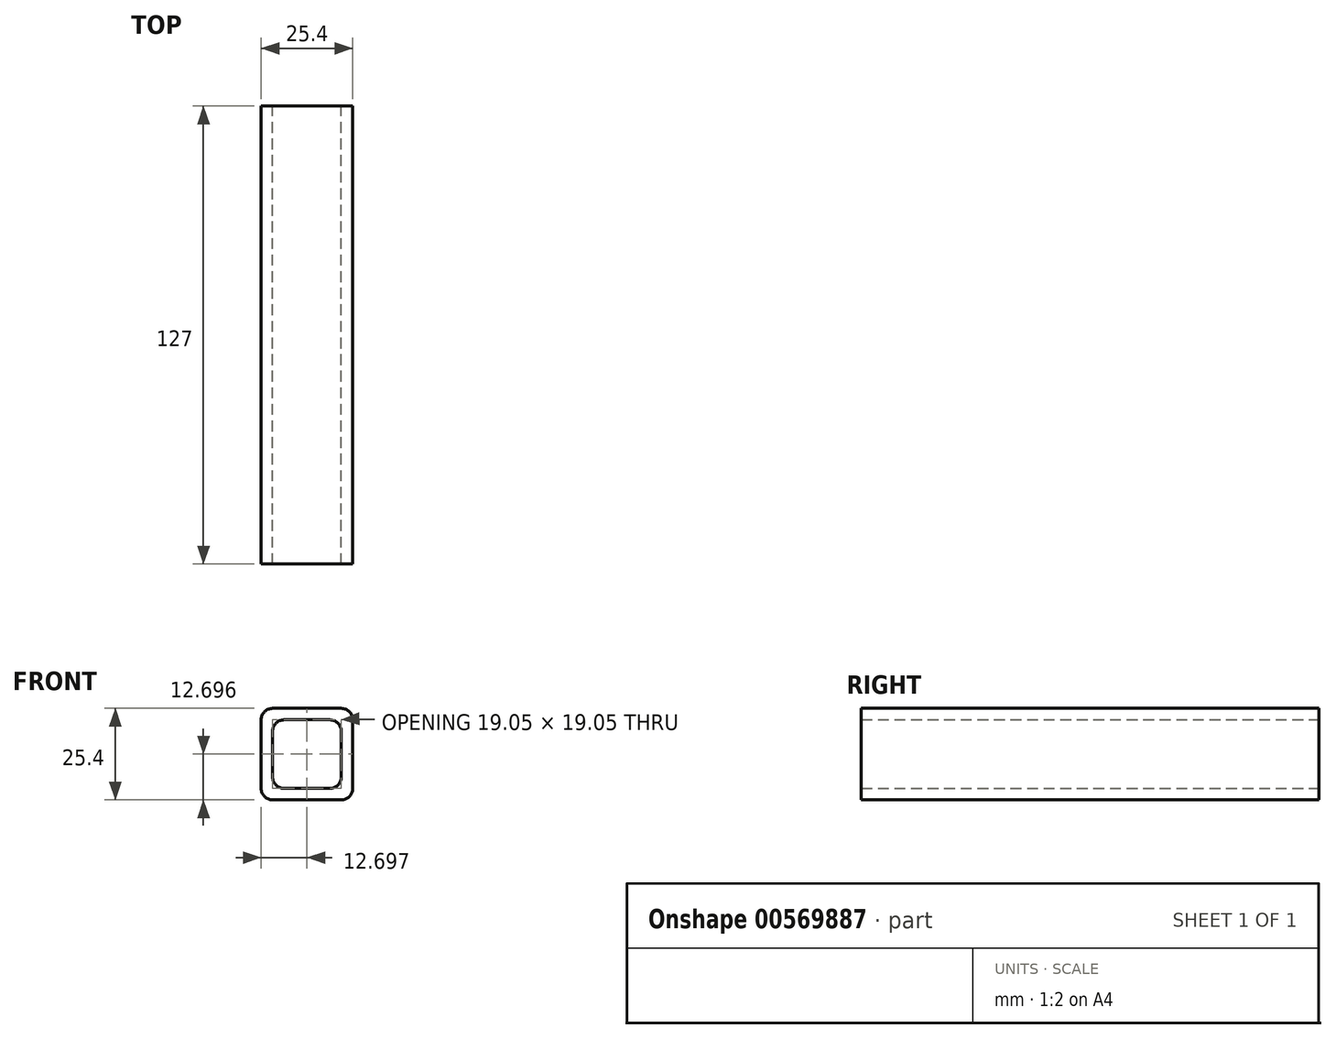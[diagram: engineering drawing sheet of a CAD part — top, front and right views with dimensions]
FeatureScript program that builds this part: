
annotation { "Feature Type Name" : "Feature", "Feature Type Description" : "" }
export const myFeature = defineFeature(function(context is Context, id is Id, definition is map)
    precondition{}
    {
        {
            var Q0;
            Q0=qCreatedBy(makeId("Front.planeOp"),FACE);
            var sketch = newSketch(context, id + "F0", { "sketchPlane" : qUnion([Q0])});
            skLineSegment(sketch, "E0.bottom", {"start": v(9.13, -13) * mm, "end": v(-9.92, -13) * mm});
            skLineSegment(sketch, "E0.top", {"start": v(9.13, 12.4) * mm, "end": v(-9.92, 12.4) * mm});
            skLineSegment(sketch, "E0.left", {"start": v(12.3, -9.82) * mm, "end": v(12.3, 9.23) * mm});
            skLineSegment(sketch, "E0.right", {"start": v(-13.1, -9.82) * mm, "end": v(-13.1, 9.23) * mm});
            skLineSegment(sketch, "E1.bottom", {"start": v(5.96, -9.82) * mm, "end": v(-6.74, -9.82) * mm});
            skLineSegment(sketch, "E1.top", {"start": v(5.96, 9.23) * mm, "end": v(-6.74, 9.23) * mm});
            skLineSegment(sketch, "E1.left", {"start": v(9.13, -6.64) * mm, "end": v(9.13, 6.06) * mm});
            skLineSegment(sketch, "E1.right", {"start": v(-9.92, -6.64) * mm, "end": v(-9.92, 6.06) * mm});
            skPoint(sketch, "E2.visualSharp", {"position": v(9.13, 9.23) * mm});
            skArc(sketch, "E2.filletArc", {"start": v(9.13, 6.06) * mm, "mid": v(8.2, 8.3) * mm, "end": v(5.96, 9.23) * mm});
            skPoint(sketch, "E3.visualSharp", {"position": v(-9.92, 9.23) * mm});
            skArc(sketch, "E3.filletArc", {"start": v(-6.74, 9.23) * mm, "mid": v(-8.99, 8.3) * mm, "end": v(-9.92, 6.06) * mm});
            skPoint(sketch, "E4.visualSharp", {"position": v(-9.92, -9.82) * mm});
            skArc(sketch, "E4.filletArc", {"start": v(-9.92, -6.64) * mm, "mid": v(-8.99, -8.89) * mm, "end": v(-6.74, -9.82) * mm});
            skPoint(sketch, "E5.visualSharp", {"position": v(9.13, -9.82) * mm});
            skArc(sketch, "E5.filletArc", {"start": v(5.96, -9.82) * mm, "mid": v(8.2, -8.89) * mm, "end": v(9.13, -6.64) * mm});
            skPoint(sketch, "E6.visualSharp", {"position": v(12.3, 12.4) * mm});
            skArc(sketch, "E6.filletArc", {"start": v(12.3, 9.23) * mm, "mid": v(11.38, 11.48) * mm, "end": v(9.13, 12.4) * mm});
            skPoint(sketch, "E7.visualSharp", {"position": v(-13.1, 12.4) * mm});
            skArc(sketch, "E7.filletArc", {"start": v(-9.92, 12.4) * mm, "mid": v(-12.16, 11.48) * mm, "end": v(-13.1, 9.23) * mm});
            skPoint(sketch, "E8.visualSharp", {"position": v(-13.1, -13) * mm});
            skArc(sketch, "E8.filletArc", {"start": v(-13.1, -9.82) * mm, "mid": v(-12.16, -12.06) * mm, "end": v(-9.92, -13) * mm});
            skPoint(sketch, "E9.visualSharp", {"position": v(12.3, -13) * mm});
            skArc(sketch, "E9.filletArc", {"start": v(9.13, -13) * mm, "mid": v(11.38, -12.06) * mm, "end": v(12.3, -9.82) * mm});
            skSolve(sketch);
        }
        {
            var Q0;
            Q0 = qSketchRegion(id + "F0", true);
            extrude(context, id + "F1", {"entities" : qUnion([Q0]), "depth" : 127 * mm, "offsetDistance" : 25.4 * mm});
        }
    });
